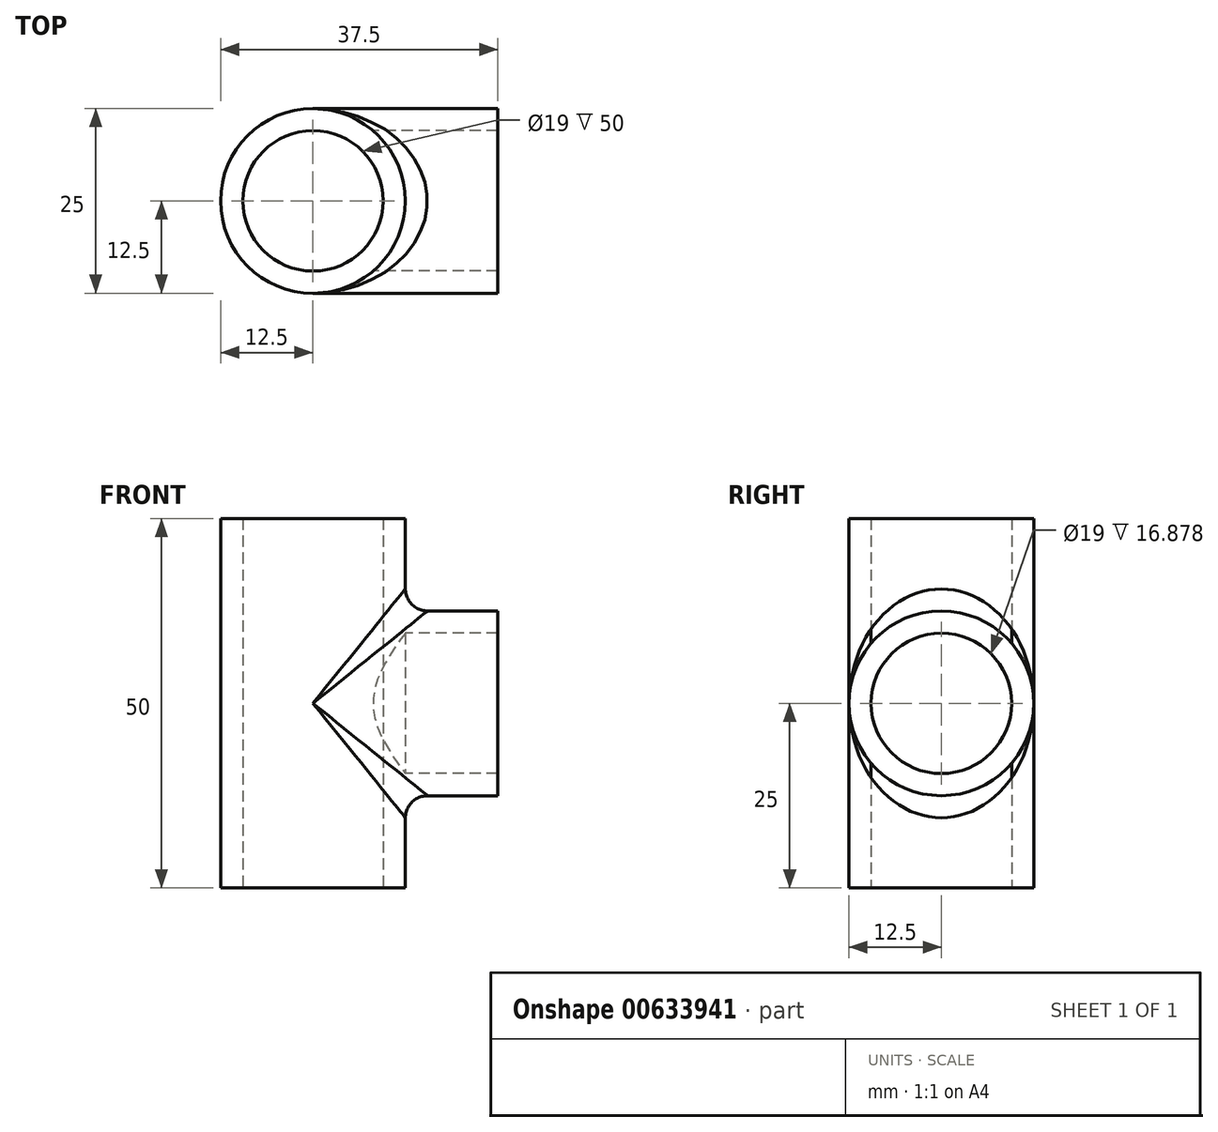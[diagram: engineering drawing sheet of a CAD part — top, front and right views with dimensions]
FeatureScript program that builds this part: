
annotation { "Feature Type Name" : "Feature", "Feature Type Description" : "" }
export const myFeature = defineFeature(function(context is Context, id is Id, definition is map)
    precondition{}
    {
        {
            var Q0;
            Q0=qCreatedBy(makeId("Top.planeOp"),FACE);
            var sketch = newSketch(context, id + "F0", { "sketchPlane" : qUnion([Q0])});
            skCircle(sketch, "E0", {"center": v(0, 0) * mm, "radius": 12.5 * mm});
            skCircle(sketch, "E1", {"center": v(0, 0) * mm, "radius": 9.5 * mm});
            skSolve(sketch);
        }
        {
            var Q0;
            Q0 = qSketchRegion(id + "F0", true);
            extrude(context, id + "F1", {"entities" : qUnion([Q0]), "depth" : 50 * mm, "offsetDistance" : 25 * mm});
        }
        {
            var Q0;
            Q0=qCreatedBy(makeId("Right.planeOp"),FACE);
            var sketch = newSketch(context, id + "F2", { "sketchPlane" : qUnion([Q0])});
            skLineSegment(sketch, "E2", {"start": v(0, 0) * mm, "end": v(0, 50) * mm});
            skCircle(sketch, "E3", {"center": v(0, 25) * mm, "radius": 12.5 * mm});
            skCircle(sketch, "E4", {"center": v(0, 25) * mm, "radius": 9.5 * mm});
            skSolve(sketch);
        }
        {
            var Q0;
            Q0 = qSketchRegion(id + "F2", true);
            extrude(context, id + "F3", {"entities" : qUnion([Q0]), "operationType" : NewBodyOperationType.ADD, "depth" : 25 * mm, "offsetDistance" : 25 * mm});
        }
        {
            var Q0;
            Q0=makeQuery(id+"F3.boolean.opBoolean","INTERSECT",EDGE,{"disambiguationData":[OD(1.0)],"derivedFrom":[makeQuery(id+"F1.opExtrude","SWEPT_FACE",FACE,{"disambiguationData":[OSD([sQuery(id+"F0.wireOp",EDGE,"E0")])]}),makeQuery(id+"F3.opExtrude","SWEPT_FACE",FACE,{"disambiguationData":[OSD([sQuery(id+"F2.wireOp",EDGE,"E3")])]})]});
            var Q1;
            Q1=makeQuery(id+"F3.boolean.opBoolean","INTERSECT",EDGE,{"disambiguationData":[OD(0.0)],"derivedFrom":[makeQuery(id+"F1.opExtrude","SWEPT_FACE",FACE,{"disambiguationData":[OSD([sQuery(id+"F0.wireOp",EDGE,"E0")])]}),makeQuery(id+"F3.opExtrude","SWEPT_FACE",FACE,{"disambiguationData":[OSD([sQuery(id+"F2.wireOp",EDGE,"E3")])]})]});
            fillet(context, id + "F4", {"entities" : qUnion([Q0, Q1]), "radius" : 3 * mm, "tangentPropagation" : true, "allowEdgeOverflow" : false});
        }
        {
            var Q0;
            Q0=qCreatedBy(makeId("Top.planeOp"),FACE);
            var sketch = newSketch(context, id + "F5", { "sketchPlane" : qUnion([Q0])});
            skCircle(sketch, "E5.0", {"center": v(0, 0) * mm, "radius": 9.5 * mm});
            skSolve(sketch);
        }
        {
            var Q0;
            Q0 = qSketchRegion(id + "F5", true);
            extrude(context, id + "F6", {"entities" : qUnion([Q0]), "operationType" : NewBodyOperationType.REMOVE, "depth" : 50 * mm, "offsetDistance" : 25 * mm});
        }
    });
